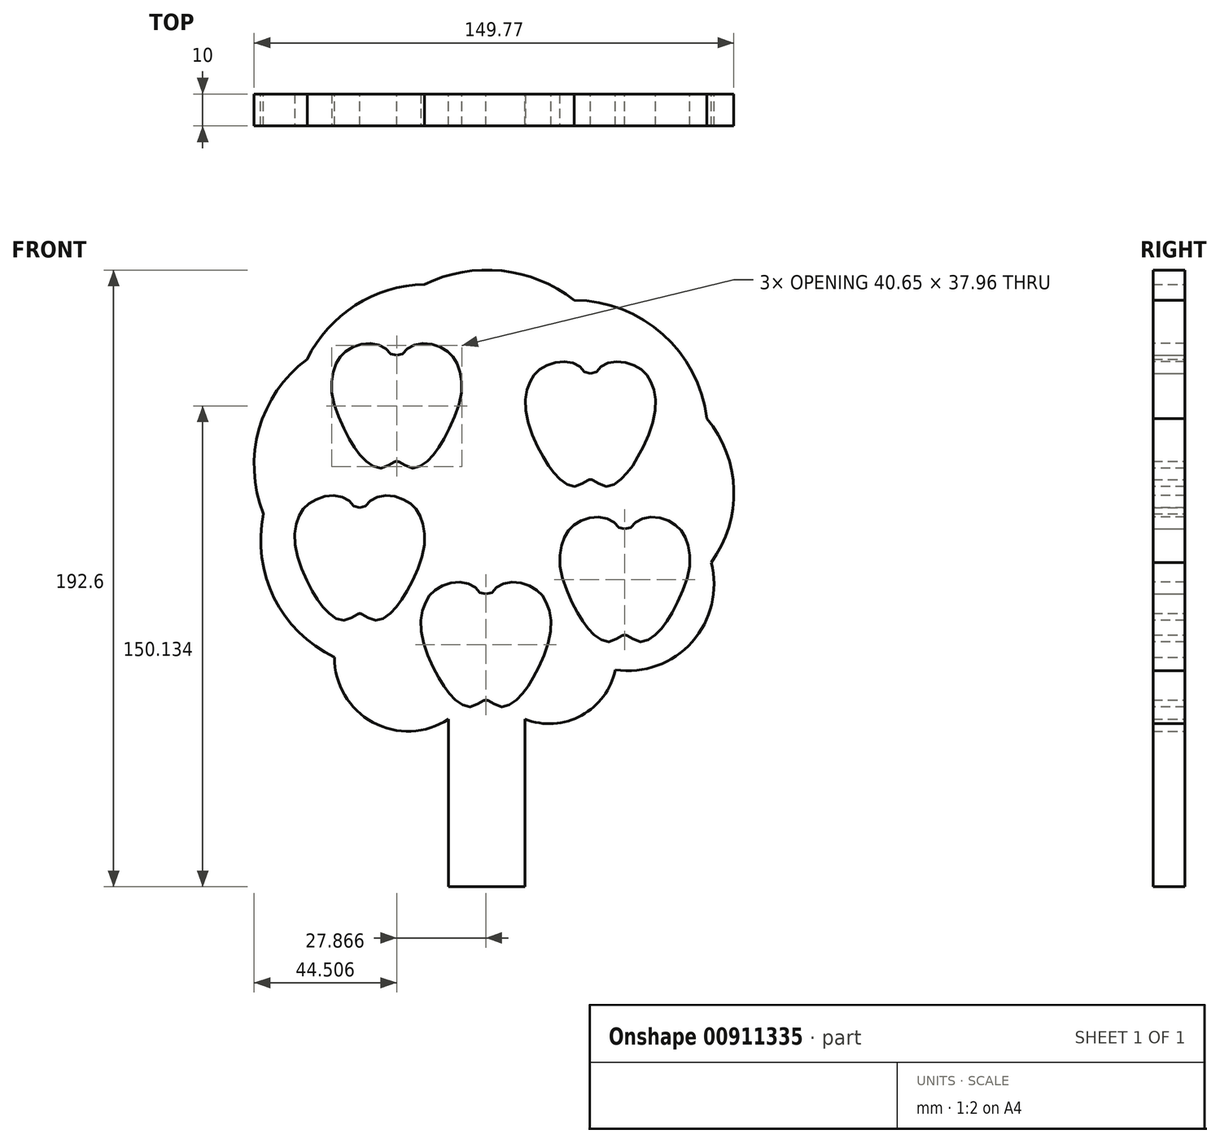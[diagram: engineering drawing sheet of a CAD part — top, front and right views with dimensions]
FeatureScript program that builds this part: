
annotation { "Feature Type Name" : "Feature", "Feature Type Description" : "" }
export const myFeature = defineFeature(function(context is Context, id is Id, definition is map)
    precondition{}
    {
        {
            var Q0;
            Q0=qCreatedBy(makeId("Front.planeOp"),FACE);
            var sketch = newSketch(context, id + "F0", { "sketchPlane" : qUnion([Q0])});
            skArc(sketch, "E0", {"start": v(-68.64, 5.46) * mm, "mid": v(-65.35, -20.8) * mm, "end": v(-46.49, -39.35) * mm});
            skArc(sketch, "E1", {"start": v(-55.02, 53.78) * mm, "mid": v(-70.04, 31.93) * mm, "end": v(-68.64, 5.46) * mm});
            skArc(sketch, "E2", {"start": v(-18.4, 77.08) * mm, "mid": v(-39.98, 70.58) * mm, "end": v(-55.02, 53.78) * mm});
            skArc(sketch, "E3", {"start": v(28.35, 72.19) * mm, "mid": v(5.68, 81.35) * mm, "end": v(-18.4, 77.08) * mm});
            skArc(sketch, "E4", {"start": v(69.75, 35.24) * mm, "mid": v(56, 61.5) * mm, "end": v(28.35, 72.19) * mm});
            skArc(sketch, "E5", {"start": v(71.08, -9.75) * mm, "mid": v(78.17, 12.97) * mm, "end": v(69.75, 35.24) * mm});
            skArc(sketch, "E6", {"start": v(41.17, -43.3) * mm, "mid": v(65.15, -34.57) * mm, "end": v(71.08, -9.75) * mm});
            skArc(sketch, "E7", {"start": v(-46.49, -39.35) * mm, "mid": v(-34.48, -59.67) * mm, "end": v(-10.9, -58.7) * mm});
            skArc(sketch, "E8", {"start": v(12.96, -58.7) * mm, "mid": v(30.62, -57.52) * mm, "end": v(41.17, -43.3) * mm});
            skLineSegment(sketch, "E9.top", {"start": v(-10.9, -111.01) * mm, "end": v(12.96, -111.01) * mm});
            skLineSegment(sketch, "E9.left", {"start": v(-10.9, -58.7) * mm, "end": v(-10.9, -111.01) * mm});
            skLineSegment(sketch, "E9.right", {"start": v(12.96, -57.73) * mm, "end": v(12.96, -111.01) * mm});
            skFitSpline(sketch, "E10", {"points": [v(-27.08, 54.96) * mm, v(-30.18, 56.84) * mm, v(-36.02, 58.68) * mm, v(-42.8, 56.3) * mm, v(-46.15, 51.9) * mm, v(-47.2, 42.66) * mm, v(-41.98, 29.06) * mm, v(-37.16, 22.41) * mm, v(-31.64, 19.72) * mm, v(-27.08, 21.84) * mm, v(-24.34, 19.35) * mm], "startDerivative": vector(-64.18, -19.37) * mm, "endDerivative": vector(35.76, -50.34) * mm});
            skFitSpline(sketch, "E11.MirrorCS", {"points": [v(-27.08, 54.96) * mm, v(-23.98, 56.84) * mm, v(-18.15, 58.68) * mm, v(-11.37, 56.3) * mm, v(-8.02, 51.9) * mm, v(-6.96, 42.66) * mm, v(-12.2, 29.06) * mm, v(-17.01, 22.41) * mm, v(-22.52, 19.72) * mm, v(-27.08, 21.84) * mm, v(-29.83, 19.35) * mm], "startDerivative": vector(64.18, -19.37) * mm, "endDerivative": vector(-35.76, -50.34) * mm});
            skFitSpline(sketch, "E12", {"points": [v(33.43, 49.3) * mm, v(30.33, 51.17) * mm, v(24.49, 53.01) * mm, v(17.72, 50.63) * mm, v(14.36, 46.23) * mm, v(13.3, 37) * mm, v(18.53, 23.4) * mm, v(23.35, 16.75) * mm, v(28.87, 14.06) * mm, v(33.43, 16.17) * mm, v(36.17, 13.69) * mm], "startDerivative": vector(-64.18, -19.37) * mm, "endDerivative": vector(35.76, -50.34) * mm});
            skFitSpline(sketch, "E13.MirrorCS", {"points": [v(33.43, 49.3) * mm, v(36.52, 51.17) * mm, v(42.36, 53.01) * mm, v(49.14, 50.63) * mm, v(52.5, 46.23) * mm, v(53.55, 37) * mm, v(48.32, 23.4) * mm, v(43.5, 16.75) * mm, v(37.99, 14.06) * mm, v(33.43, 16.17) * mm, v(30.68, 13.69) * mm], "startDerivative": vector(64.18, -19.37) * mm, "endDerivative": vector(-35.76, -50.34) * mm});
            skFitSpline(sketch, "E14", {"points": [v(-38.62, 7.42) * mm, v(-41.72, 9.3) * mm, v(-47.56, 11.14) * mm, v(-54.33, 8.76) * mm, v(-57.69, 4.36) * mm, v(-58.74, -4.88) * mm, v(-53.51, -18.48) * mm, v(-48.7, -25.13) * mm, v(-43.18, -27.82) * mm, v(-38.62, -25.7) * mm, v(-35.87, -28.19) * mm], "startDerivative": vector(-64.18, -19.37) * mm, "endDerivative": vector(35.76, -50.34) * mm});
            skFitSpline(sketch, "E15.MirrorCS", {"points": [v(-38.62, 7.42) * mm, v(-35.52, 9.3) * mm, v(-29.68, 11.14) * mm, v(-22.9, 8.76) * mm, v(-19.55, 4.36) * mm, v(-18.5, -4.88) * mm, v(-23.73, -18.48) * mm, v(-28.55, -25.13) * mm, v(-34.06, -27.82) * mm, v(-38.62, -25.7) * mm, v(-41.36, -28.19) * mm], "startDerivative": vector(64.18, -19.37) * mm, "endDerivative": vector(-35.76, -50.34) * mm});
            skFitSpline(sketch, "E16", {"points": [v(44.13, 0.72) * mm, v(41.03, 2.6) * mm, v(35.2, 4.43) * mm, v(28.42, 2.06) * mm, v(25.06, -2.34) * mm, v(24, -11.58) * mm, v(29.24, -25.18) * mm, v(34.06, -31.83) * mm, v(39.57, -34.52) * mm, v(44.13, -32.4) * mm, v(46.88, -34.9) * mm], "startDerivative": vector(-64.18, -19.37) * mm, "endDerivative": vector(35.76, -50.34) * mm});
            skFitSpline(sketch, "E17.MirrorCS", {"points": [v(44.13, 0.72) * mm, v(47.23, 2.6) * mm, v(53.07, 4.43) * mm, v(59.84, 2.06) * mm, v(63.2, -2.34) * mm, v(64.25, -11.58) * mm, v(59.02, -25.18) * mm, v(54.2, -31.83) * mm, v(48.7, -34.52) * mm, v(44.13, -32.4) * mm, v(41.39, -34.9) * mm], "startDerivative": vector(64.18, -19.37) * mm, "endDerivative": vector(-35.76, -50.34) * mm});
            skFitSpline(sketch, "E18", {"points": [v(0.78, -19.6) * mm, v(-2.32, -17.73) * mm, v(-8.15, -15.89) * mm, v(-14.93, -18.27) * mm, v(-18.29, -22.67) * mm, v(-19.34, -31.9) * mm, v(-14.11, -45.5) * mm, v(-9.3, -52.15) * mm, v(-3.78, -54.84) * mm, v(0.78, -52.73) * mm, v(3.53, -55.21) * mm], "startDerivative": vector(-64.18, -19.37) * mm, "endDerivative": vector(35.76, -50.34) * mm});
            skFitSpline(sketch, "E19.MirrorCS", {"points": [v(0.78, -19.6) * mm, v(3.88, -17.73) * mm, v(9.72, -15.89) * mm, v(16.5, -18.27) * mm, v(19.85, -22.67) * mm, v(20.9, -31.9) * mm, v(15.67, -45.5) * mm, v(10.85, -52.15) * mm, v(5.34, -54.84) * mm, v(0.78, -52.73) * mm, v(-1.96, -55.21) * mm], "startDerivative": vector(64.18, -19.37) * mm, "endDerivative": vector(-35.76, -50.34) * mm});
            skSolve(sketch);
        }
        {
            var Q0;
            Q0 = qSketchRegion(id + "F0", true);
            extrude(context, id + "F1", {"entities" : qUnion([Q0]), "depth" : 10 * mm, "offsetDistance" : 25 * mm});
        }
    });
